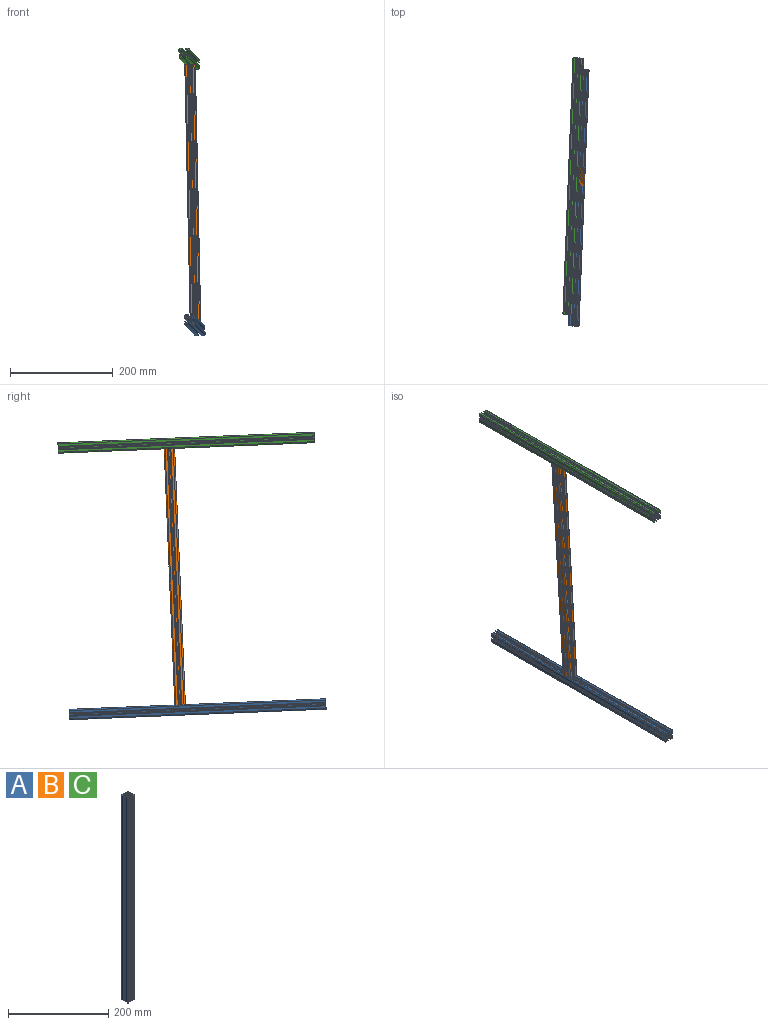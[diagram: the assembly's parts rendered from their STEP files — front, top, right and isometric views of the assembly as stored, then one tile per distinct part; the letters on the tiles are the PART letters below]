
ASSEMBLY  parts=3 mates=2
PART A: 75 faces, bbox 20x20x500 mm
  f0: plane 500x0.7mm, normal (0,1,0), area 350mm2, adj f1,f72,f73,f74
  f1: cylinder r=0.8mm len=500mm, axis (0,0,-1), area 628.3mm2, adj f0,f2,f73,f74
  f2: plane 500x4.7mm, normal (-1,0,0), area 2350mm2, adj f1,f3,f73,f74
  f3: cylinder r=2mm len=500mm, axis (0,0,-1), area 1570.8mm2, adj f2,f4,f73,f74
  f4: plane 500x4.7mm, normal (0,-1,0), area 2350mm2, adj f3,f5,f73,f74
  f5: cylinder r=0.8mm len=500mm, axis (0,0,-1), area 628.3mm2, adj f4,f6,f73,f74
  f6: plane 500x0.7mm, normal (1,0,0), area 350mm2, adj f5,f7,f73,f74
  f7: cylinder r=0.3mm len=500mm, axis (0,0,-1), area 235.6mm2, adj f6,f8,f73,f74
  f8: plane 500x2.12mm, normal (0,1,0), area 1058.8mm2, adj f7,f9,f73,f74
  f9: cylinder r=0.83mm len=500mm, axis (0,0,-1), area 980.7mm2, adj f8,f10,f73,f74
  f10: plane 500x2.25mm, normal (0.71,-0.71,0), area 1591.2mm2, adj f9,f11,f73,f74
  f11: cylinder r=3mm len=500mm, axis (0,0,-1), area 1178.1mm2, adj f10,f12,f73,f74
  f12: plane 500x2.27mm, normal (0,-1,0), area 1134.6mm2, adj f11,f13,f73,f74
  f13: cylinder r=3mm len=500mm, axis (0,0,-1), area 1178.1mm2, adj f12,f14,f73,f74
  f14: plane 500x2.25mm, normal (-0.71,-0.71,0), area 1591.2mm2, adj f13,f15,f73,f74
  f15: cylinder r=0.83mm len=500mm, axis (0,0,-1), area 980.7mm2, adj f14,f16,f73,f74
  f16: plane 500x2.12mm, normal (0,1,0), area 1058.8mm2, adj f15,f17,f73,f74
  f17: cylinder r=0.3mm len=500mm, axis (0,0,-1), area 235.6mm2, adj f16,f18,f73,f74
  f18: plane 500x0.7mm, normal (-1,0,0), area 350mm2, adj f17,f19,f73,f74
  f19: cylinder r=0.8mm len=500mm, axis (0,0,-1), area 628.3mm2, adj f18,f20,f73,f74
  f20: plane 500x4.7mm, normal (0,-1,0), area 2350mm2, adj f19,f21,f73,f74
  f21: cylinder r=2mm len=500mm, axis (0,0,-1), area 1570.8mm2, adj f20,f22,f73,f74
  f22: plane 500x4.7mm, normal (1,0,0), area 2350mm2, adj f21,f23,f73,f74
  f23: cylinder r=0.8mm len=500mm, axis (0,0,-1), area 628.3mm2, adj f22,f24,f73,f74
  f24: plane 500x0.7mm, normal (0,1,0), area 350mm2, adj f23,f25,f73,f74
  f25: cylinder r=0.3mm len=500mm, axis (0,0,-1), area 235.6mm2, adj f24,f26,f73,f74
  f26: plane 500x2.12mm, normal (-1,0,0), area 1058.8mm2, adj f25,f27,f73,f74
  f27: cylinder r=0.83mm len=500mm, axis (0,0,-1), area 980.7mm2, adj f26,f28,f73,f74
  f28: plane 500x2.25mm, normal (0.71,0.71,0), area 1591.2mm2, adj f27,f29,f73,f74
  f29: cylinder r=3mm len=500mm, axis (0,0,-1), area 1178.1mm2, adj f28,f30,f73,f74
  f30: plane 500x2.27mm, normal (1,0,0), area 1134.6mm2, adj f29,f31,f73,f74
  f31: cylinder r=3mm len=500mm, axis (0,0,-1), area 1178.1mm2, adj f30,f32,f73,f74
  f32: plane 500x2.25mm, normal (0.71,-0.71,0), area 1591.2mm2, adj f31,f33,f73,f74
  f33: cylinder r=0.83mm len=500mm, axis (0,0,-1), area 980.7mm2, adj f32,f34,f73,f74
  f34: plane 500x2.12mm, normal (-1,0,0), area 1058.8mm2, adj f33,f35,f73,f74
  f35: cylinder r=0.3mm len=500mm, axis (0,0,-1), area 235.6mm2, adj f34,f36,f73,f74
  f36: plane 500x0.7mm, normal (0,-1,0), area 350mm2, adj f35,f37,f73,f74
  f37: cylinder r=0.8mm len=500mm, axis (0,0,-1), area 628.3mm2, adj f36,f38,f73,f74
  f38: plane 500x4.7mm, normal (1,0,0), area 2350mm2, adj f37,f39,f73,f74
  f39: cylinder r=2mm len=500mm, axis (0,0,-1), area 1570.8mm2, adj f38,f40,f73,f74
  f40: plane 500x4.7mm, normal (0,1,0), area 2350mm2, adj f39,f41,f73,f74
  f41: cylinder r=0.8mm len=500mm, axis (0,0,-1), area 628.3mm2, adj f40,f42,f73,f74
  f42: plane 500x0.7mm, normal (-1,0,0), area 350mm2, adj f41,f43,f73,f74
  f43: cylinder r=0.3mm len=500mm, axis (0,0,-1), area 235.6mm2, adj f42,f44,f73,f74
  f44: plane 500x2.12mm, normal (0,-1,0), area 1058.8mm2, adj f43,f45,f73,f74
  f45: cylinder r=0.83mm len=500mm, axis (0,0,-1), area 980.7mm2, adj f44,f46,f73,f74
  f46: plane 500x2.25mm, normal (-0.71,0.71,0), area 1591.2mm2, adj f45,f47,f73,f74
  f47: cylinder r=3mm len=500mm, axis (0,0,-1), area 1178.1mm2, adj f46,f48,f73,f74
  f48: plane 500x2.27mm, normal (0,1,0), area 1134.6mm2, adj f47,f49,f73,f74
  f49: cylinder r=3mm len=500mm, axis (0,0,-1), area 1178.1mm2, adj f48,f50,f73,f74
  f50: plane 500x2.25mm, normal (0.71,0.71,0), area 1591.2mm2, adj f49,f51,f73,f74
  f51: cylinder r=0.83mm len=500mm, axis (0,0,-1), area 980.7mm2, adj f50,f52,f73,f74
  f52: plane 500x2.12mm, normal (0,-1,0), area 1058.8mm2, adj f51,f53,f73,f74
  f53: cylinder r=0.3mm len=500mm, axis (0,0,-1), area 235.6mm2, adj f52,f54,f73,f74
  f54: plane 500x0.7mm, normal (1,0,0), area 350mm2, adj f53,f55,f73,f74
  f55: cylinder r=0.8mm len=500mm, axis (0,0,-1), area 628.3mm2, adj f54,f56,f73,f74
  f56: plane 500x4.7mm, normal (0,1,0), area 2350mm2, adj f55,f57,f73,f74
  f57: cylinder r=2mm len=500mm, axis (0,0,-1), area 1570.8mm2, adj f56,f58,f73,f74
  f58: plane 500x4.7mm, normal (-1,0,0), area 2350mm2, adj f57,f59,f73,f74
  f59: cylinder r=0.8mm len=500mm, axis (0,0,-1), area 628.3mm2, adj f58,f60,f73,f74
  f60: plane 500x0.7mm, normal (0,-1,0), area 350mm2, adj f59,f61,f73,f74
  f61: cylinder r=0.3mm len=500mm, axis (0,0,-1), area 235.6mm2, adj f60,f62,f73,f74
  f62: plane 500x2.12mm, normal (1,0,0), area 1058.8mm2, adj f61,f63,f73,f74
  f63: cylinder r=0.83mm len=500mm, axis (0,0,-1), area 980.7mm2, adj f62,f64,f73,f74
  f64: plane 500x2.25mm, normal (-0.71,-0.71,0), area 1591.2mm2, adj f63,f65,f73,f74
  f65: cylinder r=3mm len=500mm, axis (0,0,-1), area 1178.1mm2, adj f64,f66,f73,f74
  f66: plane 500x2.27mm, normal (-1,0,0), area 1134.6mm2, adj f65,f67,f73,f74
  f67: cylinder r=3mm len=500mm, axis (0,0,-1), area 1178.1mm2, adj f66,f68,f73,f74
  f68: plane 500x2.25mm, normal (-0.71,0.71,0), area 1591.2mm2, adj f67,f69,f73,f74
  f69: cylinder r=0.83mm len=500mm, axis (0,0,-1), area 980.7mm2, adj f68,f70,f73,f74
  f70: plane 500x2.12mm, normal (1,0,0), area 1058.8mm2, adj f69,f72,f73,f74
  f71: cylinder r=2.15mm len=500mm, axis (0,0,-1), area 6754.4mm2, adj f73,f74
  f72: cylinder r=0.3mm len=500mm, axis (0,0,-1), area 235.6mm2, adj f0,f70,f73,f74
  f73: plane 20x20mm, normal (0,0,1), area 183.9mm2, adj f0,f1,f2,f3,f4,f5,f6,f7
  f74: plane 20x20mm, normal (0,0,-1), area 183.9mm2, adj f0,f1,f2,f3,f4,f5,f6,f7
PART B: same geometry as A
PART C: same geometry as A
PLACE A rot(axis=(-0.02,-0.69,0.72),179.3deg) t=(-81.77,237.34,-187.93)mm
PLACE B rot(axis=(0.72,0.69,-0.01),177.4deg) t=(-100.9,42.77,330.38)mm
PLACE C rot(axis=(-0.02,-0.69,0.72),179.3deg) t=(-92.74,259.13,331.49)mm
MATE planar C.f40 <-> B.f3  axis (0.02,-0.04,-1) through (-108.01,9.33,331.64)mm
MATE planar A.f20 <-> B.f39  axis (-0.02,0.04,1) through (-97.46,-11.62,-167.81)mm
